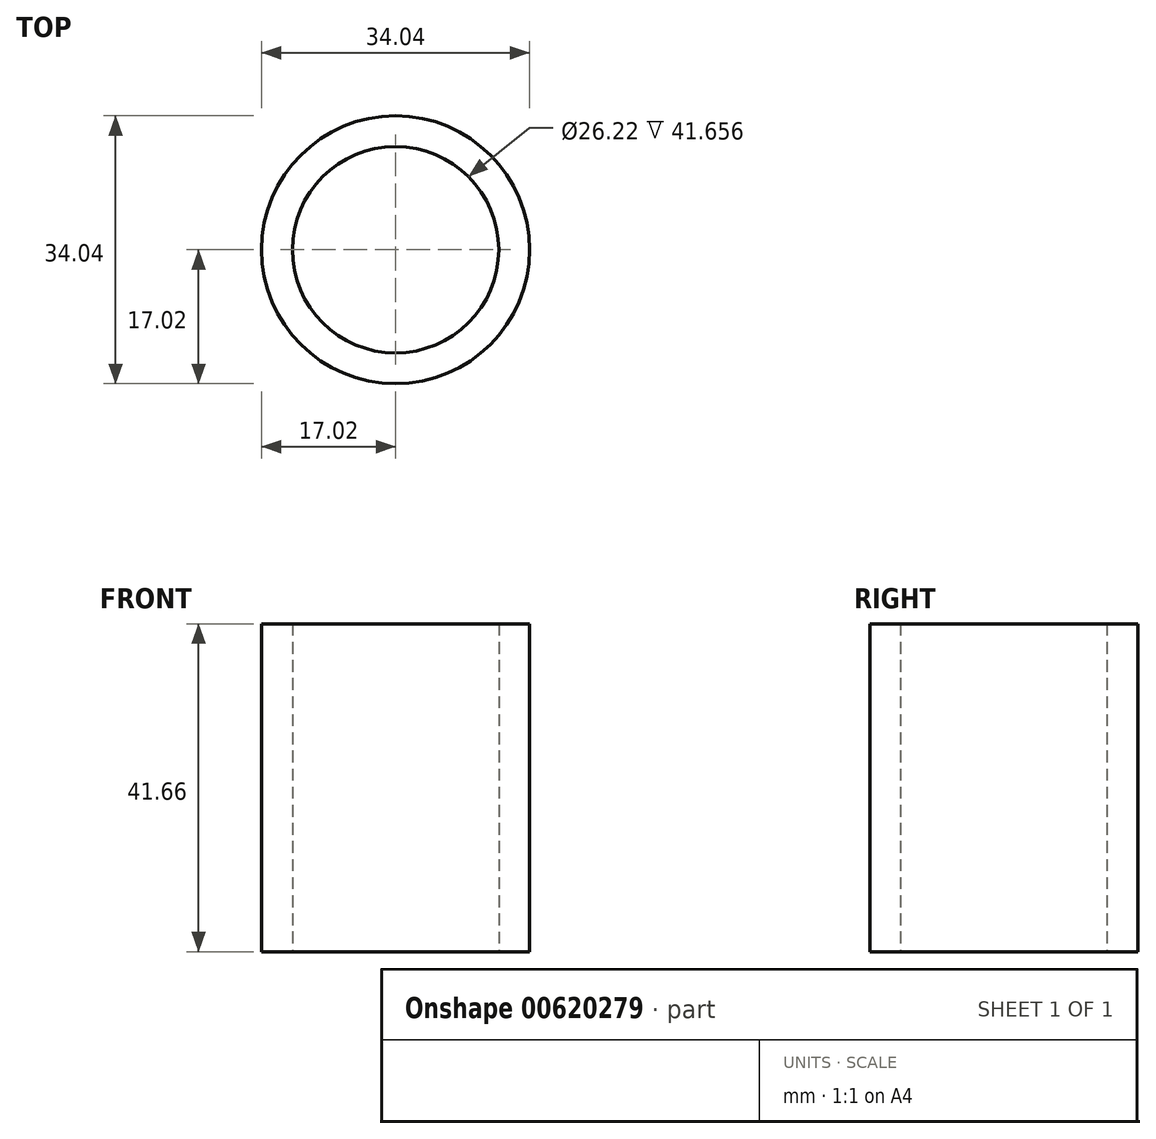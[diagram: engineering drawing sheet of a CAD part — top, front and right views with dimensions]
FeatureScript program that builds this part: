
annotation { "Feature Type Name" : "Feature", "Feature Type Description" : "" }
export const myFeature = defineFeature(function(context is Context, id is Id, definition is map)
    precondition{}
    {
        {
            var Q0;
            Q0=qCreatedBy(makeId("Top.planeOp"),FACE);
            var sketch = newSketch(context, id + "F0", { "sketchPlane" : qUnion([Q0])});
            skCircle(sketch, "E0", {"center": v(0, 0) * mm, "radius": 17.02 * mm});
            skCircle(sketch, "E1", {"center": v(0, 0) * mm, "radius": 13.11 * mm});
            skSolve(sketch);
        }
        {
            var Q0;
            Q0 = qSketchRegion(id + "F0", true);
            extrude(context, id + "F1", {"entities" : qUnion([Q0]), "depth" : 41.66 * mm, "offsetDistance" : 25.4 * mm});
        }
    });
